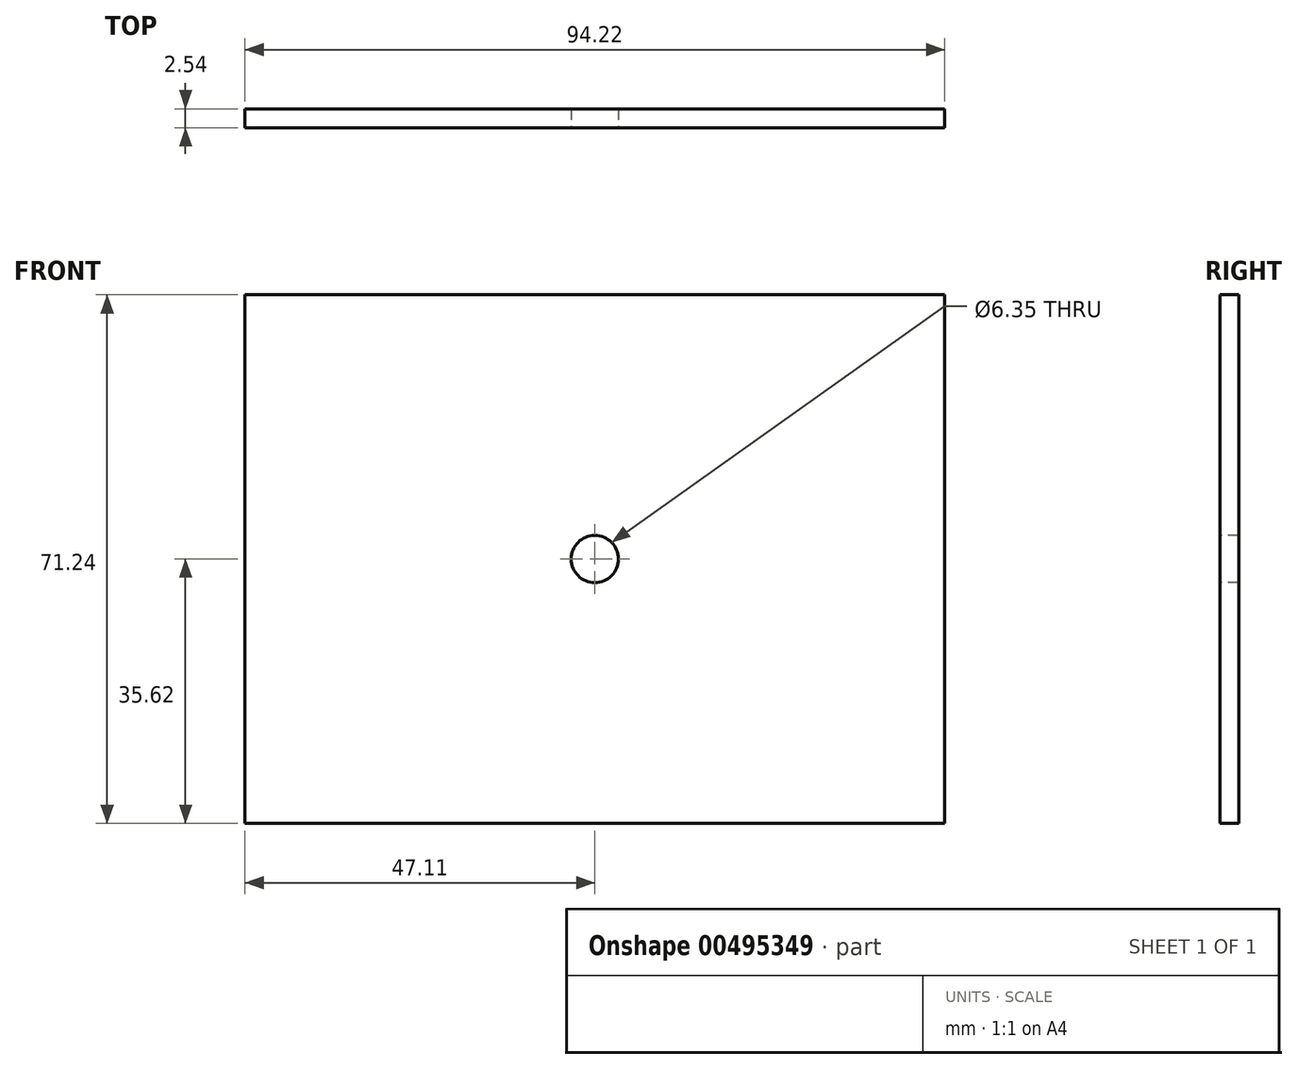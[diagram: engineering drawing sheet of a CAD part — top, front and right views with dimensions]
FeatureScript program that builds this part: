
annotation { "Feature Type Name" : "Feature", "Feature Type Description" : "" }
export const myFeature = defineFeature(function(context is Context, id is Id, definition is map)
    precondition{}
    {
        {
            var Q0;
            Q0=qCreatedBy(makeId("Front.planeOp"),FACE);
            var sketch = newSketch(context, id + "F0", { "sketchPlane" : qUnion([Q0])});
            skLineSegment(sketch, "E0.bottom", {"start": v(47.11, 35.62) * mm, "end": v(-47.11, 35.62) * mm});
            skLineSegment(sketch, "E0.top", {"start": v(47.11, -35.62) * mm, "end": v(-47.11, -35.62) * mm});
            skLineSegment(sketch, "E0.left", {"start": v(47.11, 35.62) * mm, "end": v(47.11, -35.62) * mm});
            skLineSegment(sketch, "E0.right", {"start": v(-47.11, 35.62) * mm, "end": v(-47.11, -35.62) * mm});
            skPoint(sketch, "E0.middle", {"position": v(0, 0) * mm});
            skSolve(sketch);
        }
        {
            var Q0;
            Q0=makeQuery(id+"F0.imprint","IMPRINT",FACE,{"disambiguationData":[TD([[makeQuery(id+"F0.imprint","IMPRINT",EDGE,{"derivedFrom":sQuery(id+"F0.wireOp",EDGE,"E0.bottom")}),1.0]])]});
            extrude(context, id + "F1", {"entities" : qUnion([Q0]), "depth" : 2.54 * mm});
        }
        {
            var Q0;
            Q0=makeQuery(id+"F1.opExtrude","CAP_FACE",FACE,{"disambiguationData":[OSD([sQuery(id+"F0.wireOp",EDGE,"E0.bottom"),sQuery(id+"F0.wireOp",EDGE,"E0.top"),sQuery(id+"F0.wireOp",EDGE,"E0.left"),sQuery(id+"F0.wireOp",EDGE,"E0.right")])],"isStart":false});
            var sketch = newSketch(context, id + "F2", { "sketchPlane" : qUnion([Q0])});
            skCircle(sketch, "E1", {"center": v(0, 0) * mm, "radius": 3.18 * mm});
            skSolve(sketch);
        }
        {
            var Q0;
            Q0=makeQuery(id+"F2.imprint","IMPRINT",FACE,{"disambiguationData":[TD([[makeQuery(id+"F2.imprint","IMPRINT",EDGE,{"derivedFrom":sQuery(id+"F2.wireOp",EDGE,"E1")}),1.0]])]});
            extrude(context, id + "F3", {"entities" : qUnion([Q0]), "operationType" : NewBodyOperationType.REMOVE, "endBound" : BoundingType.UP_TO_NEXT, "oppositeDirection" : true, "depth" : 25.4 * mm});
        }
    });
